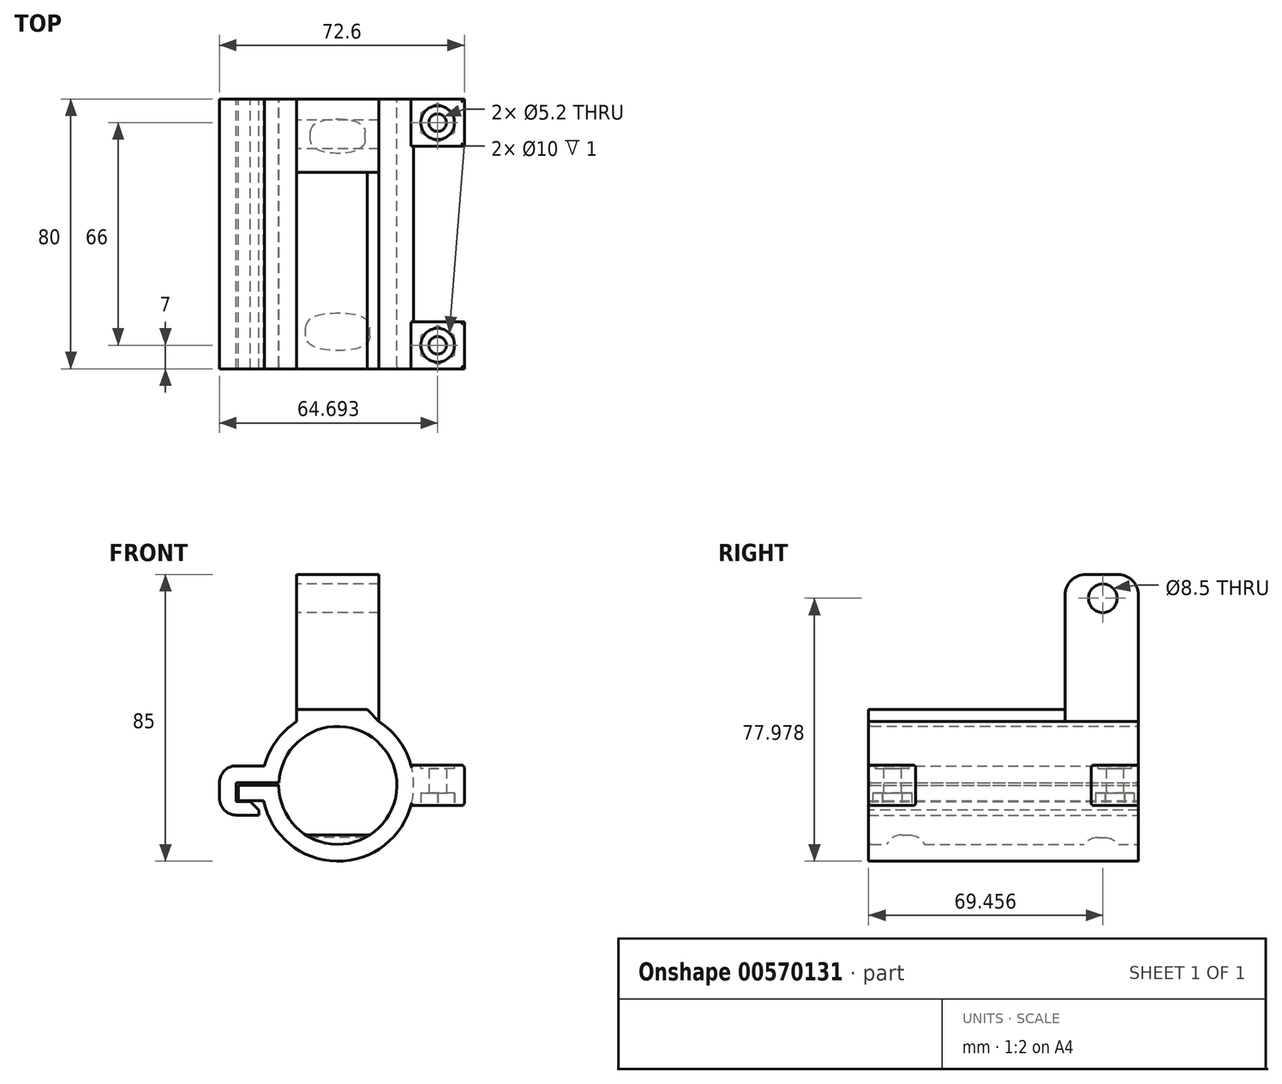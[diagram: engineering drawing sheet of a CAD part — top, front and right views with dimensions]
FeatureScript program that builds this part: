
annotation { "Feature Type Name" : "Feature", "Feature Type Description" : "" }
export const myFeature = defineFeature(function(context is Context, id is Id, definition is map)
    precondition{}
    {
        {
            var Q0;
            Q0=qCreatedBy(makeId("Front.planeOp"),FACE);
            var sketch = newSketch(context, id + "F0", { "sketchPlane" : qUnion([Q0])});
            skCircle(sketch, "E0", {"center": v(0, 0) * mm, "radius": 17.5 * mm});
            skCircle(sketch, "E1", {"center": v(0, 0) * mm, "radius": 22.5 * mm});
            skLineSegment(sketch, "E2", {"start": v(-22.5, 0) * mm, "end": v(22.5, 0) * mm});
            skLineSegment(sketch, "E3", {"start": v(22.5, 0) * mm, "end": v(37.5, 0) * mm});
            skLineSegment(sketch, "E4", {"start": v(37.5, 0) * mm, "end": v(37.5, -6) * mm});
            skLineSegment(sketch, "E5", {"start": v(37.5, -6) * mm, "end": v(21.69, -6) * mm});
            skLineSegment(sketch, "E6.MirrorCS", {"start": v(37.5, 6) * mm, "end": v(21.69, 6) * mm});
            skLineSegment(sketch, "E7.MirrorCS", {"start": v(37.5, 0) * mm, "end": v(37.5, 6) * mm});
            skLineSegment(sketch, "E8", {"start": v(-22.5, 0) * mm, "end": v(-29.5, 0) * mm});
            skLineSegment(sketch, "E9", {"start": v(-29.5, 0) * mm, "end": v(-29.5, -4.6) * mm});
            skLineSegment(sketch, "E10", {"start": v(-29.5, -4.6) * mm, "end": v(-22.02, -4.6) * mm});
            skLineSegment(sketch, "E11", {"start": v(-30.1, -4.8) * mm, "end": v(-30.1, 0.8) * mm});
            skLineSegment(sketch, "E12", {"start": v(-30.1, 0.8) * mm, "end": v(-22.49, 0.8) * mm});
            skLineSegment(sketch, "E13", {"start": v(-30.1, -4.8) * mm, "end": v(-23.4, -4.8) * mm});
            skLineSegment(sketch, "E14", {"start": v(-23.4, -4.8) * mm, "end": v(-23.4, -8.8) * mm});
            skLineSegment(sketch, "E15", {"start": v(-23.4, -8.8) * mm, "end": v(-35.1, -8.8) * mm});
            skLineSegment(sketch, "E16", {"start": v(-35.1, -8.8) * mm, "end": v(-35.1, 5.8) * mm});
            skLineSegment(sketch, "E17", {"start": v(-35.1, 5.8) * mm, "end": v(-21.74, 5.8) * mm});
            skLineSegment(sketch, "E18", {"start": v(-22.49, 0.8) * mm, "end": v(-17.48, 0.8) * mm});
            skSolve(sketch);
        }
        {
            var Q0;
            {var subQ0=sQuery(id+"F0.wireOp",EDGE,"E8");Q0=makeQuery(id+"F0.imprint","IMPRINT",FACE,{"disambiguationData":[TD([[makeQuery(id+"F0.imprint","IMPRINT",EDGE,{"derivedFrom":subQ0}),1.0]])]});}
            var Q1;
            {var subQ0=sQuery(id+"F0.wireOp",EDGE,"E2");var subQ6=sQuery(id+"F0.wireOp",EDGE,"E0");var subQ7=makeQuery(id+"F0.imprint","INTERSECT",VERTEX,{"disambiguationData":[OD(0.0)],"derivedFrom":[subQ6,subQ0]});Q1=makeQuery(id+"F0.imprint","IMPRINT",FACE,{"disambiguationData":[TD([[makeQuery(id+"F0.imprint","IMPRINT",EDGE,{"disambiguationData":[TD([[subQ7,1.0]])],"derivedFrom":subQ6}),-1.0]])]});}
            extrude(context, id + "F1", {"entities" : qUnion([Q0, Q1]), "depth" : 80 * mm, "offsetDistance" : 25 * mm});
        }
        {
            var Q0;
            Q0=makeQuery(id+"F0.imprint","IMPRINT",FACE,{"disambiguationData":[TD([[makeQuery(id+"F0.imprint","IMPRINT",EDGE,{"derivedFrom":sQuery(id+"F0.wireOp",EDGE,"E11")}),1.0]])]});
            var Q1;
            {var subQ5=sQuery(id+"F0.wireOp",EDGE,"E18");Q1=makeQuery(id+"F0.imprint","IMPRINT",FACE,{"disambiguationData":[TD([[makeQuery(id+"F0.imprint","IMPRINT",EDGE,{"derivedFrom":subQ5}),1.0]])]});}
            extrude(context, id + "F2", {"entities" : qUnion([Q0, Q1]), "depth" : 80 * mm, "offsetDistance" : 25 * mm});
        }
        {
            var Q0;
            {var subQ0=sQuery(id+"F0.wireOp",EDGE,"E3");Q0=makeQuery(id+"F0.imprint","IMPRINT",FACE,{"disambiguationData":[TD([[makeQuery(id+"F0.imprint","IMPRINT",EDGE,{"derivedFrom":subQ0}),1.0]])]});}
            extrude(context, id + "F3", {"entities" : qUnion([Q0]), "operationType" : NewBodyOperationType.ADD, "depth" : 80 * mm, "offsetDistance" : 25 * mm, "hasSecondDirection" : true, "secondDirectionOppositeDirection" : false, "secondDirectionDepth" : 66 * mm});
        }
        {
            var Q0;
            {var subQ0=sQuery(id+"F0.wireOp",EDGE,"E3");Q0=makeQuery(id+"F0.imprint","IMPRINT",FACE,{"disambiguationData":[TD([[makeQuery(id+"F0.imprint","IMPRINT",EDGE,{"derivedFrom":subQ0}),1.0]])]});}
            extrude(context, id + "F4", {"entities" : qUnion([Q0]), "operationType" : NewBodyOperationType.ADD, "depth" : 14 * mm, "offsetDistance" : 25 * mm});
        }
        {
            var Q0;
            Q0=makeQuery(id+"F0.imprint","IMPRINT",FACE,{"disambiguationData":[TD([[makeQuery(id+"F0.imprint","IMPRINT",EDGE,{"derivedFrom":sQuery(id+"F0.wireOp",EDGE,"E4")}),-1.0]])]});
            extrude(context, id + "F5", {"entities" : qUnion([Q0]), "operationType" : NewBodyOperationType.ADD, "depth" : 80 * mm, "offsetDistance" : 25 * mm, "hasSecondDirection" : true, "secondDirectionOppositeDirection" : false, "secondDirectionDepth" : 66 * mm});
        }
        {
            var Q0;
            Q0=makeQuery(id+"F0.imprint","IMPRINT",FACE,{"disambiguationData":[TD([[makeQuery(id+"F0.imprint","IMPRINT",EDGE,{"derivedFrom":sQuery(id+"F0.wireOp",EDGE,"E4")}),-1.0]])]});
            extrude(context, id + "F6", {"entities" : qUnion([Q0]), "operationType" : NewBodyOperationType.ADD, "depth" : 14 * mm, "offsetDistance" : 25 * mm});
        }
        {
            var Q0;
            Q0=qCreatedBy(makeId("Right.planeOp"),FACE);
            var sketch = newSketch(context, id + "F7", { "sketchPlane" : qUnion([Q0])});
            skLineSegment(sketch, "E19.0", {"start": v(-80, 0) * mm, "end": v(-80, -17.5) * mm});
            skLineSegment(sketch, "E20.0", {"start": v(0, -17.5) * mm, "end": v(0, 17.5) * mm});
            skLineSegment(sketch, "E21", {"start": v(-80, -17.5) * mm, "end": v(-69, -17.5) * mm});
            skLineSegment(sketch, "E22", {"start": v(-69, -17.5) * mm, "end": v(-69, -14.7) * mm});
            skLineSegment(sketch, "E23", {"start": v(-69, -14.7) * mm, "end": v(-63, -14.7) * mm});
            skLineSegment(sketch, "E24", {"start": v(-63, -14.7) * mm, "end": v(-63, -17.5) * mm});
            skLineSegment(sketch, "E25", {"start": v(-69, -14.7) * mm, "end": v(-75, -14.7) * mm});
            skLineSegment(sketch, "E26", {"start": v(-75, -14.7) * mm, "end": v(-75, -17.5) * mm});
            skLineSegment(sketch, "E27", {"start": v(-63, -17.5) * mm, "end": v(-69, -17.5) * mm});
            skLineSegment(sketch, "E28", {"start": v(0, -17.5) * mm, "end": v(-11, -17.5) * mm});
            skLineSegment(sketch, "E29", {"start": v(-11, -17.5) * mm, "end": v(-11, -15.5) * mm});
            skLineSegment(sketch, "E30", {"start": v(-11, -15.5) * mm, "end": v(-5, -15.5) * mm});
            skLineSegment(sketch, "E31", {"start": v(-11, -15.5) * mm, "end": v(-17, -15.5) * mm});
            skLineSegment(sketch, "E32", {"start": v(-17, -15.5) * mm, "end": v(-17, -17.5) * mm});
            skLineSegment(sketch, "E33", {"start": v(-17, -17.5) * mm, "end": v(-11, -17.5) * mm});
            skLineSegment(sketch, "E34", {"start": v(-5, -15.5) * mm, "end": v(-5, -17.5) * mm});
            skSolve(sketch);
        }
        {
            var Q0;
            {var subQ0=sQuery(id+"F7.wireOp",EDGE,"E22");Q0=makeQuery(id+"F7.imprint","IMPRINT",FACE,{"disambiguationData":[TD([[makeQuery(id+"F7.imprint","IMPRINT",EDGE,{"derivedFrom":subQ0}),1.0]])]});}
            var Q1;
            Q1=makeQuery(id+"F7.imprint","IMPRINT",FACE,{"disambiguationData":[TD([[makeQuery(id+"F7.imprint","IMPRINT",EDGE,{"derivedFrom":sQuery(id+"F7.wireOp",EDGE,"E22")}),-1.0]])]});
            var Q2;
            Q2=makeQuery(id+"F7.imprint","IMPRINT",FACE,{"disambiguationData":[TD([[makeQuery(id+"F7.imprint","IMPRINT",EDGE,{"derivedFrom":sQuery(id+"F7.wireOp",EDGE,"E29")}),1.0]])]});
            var Q3;
            {var subQ0=sQuery(id+"F7.wireOp",EDGE,"E29");Q3=makeQuery(id+"F7.imprint","IMPRINT",FACE,{"disambiguationData":[TD([[makeQuery(id+"F7.imprint","IMPRINT",EDGE,{"derivedFrom":subQ0}),-1.0]])]});}
            extrude(context, id + "F8", {"entities" : qUnion([Q0, Q1, Q2, Q3]), "operationType" : NewBodyOperationType.ADD, "depth" : 9.5 * mm, "offsetDistance" : 25 * mm, "hasSecondDirection" : true, "secondDirectionOppositeDirection" : true, "secondDirectionDepth" : 9.5 * mm});
        }
        {
            var Q0;
            Q0=makeQuery(id+"F8.opExtrude","SWEPT_EDGE",EDGE,{"disambiguationData":[OSD([sQuery(id+"F7.wireOp",EDGE,"E25"),sQuery(id+"F7.wireOp",EDGE,"E26")])]});
            var Q1;
            Q1=makeQuery(id+"F8.opExtrude","SWEPT_EDGE",EDGE,{"disambiguationData":[OSD([sQuery(id+"F7.wireOp",EDGE,"E23"),sQuery(id+"F7.wireOp",EDGE,"E24")])]});
            var Q2;
            Q2=makeQuery(id+"F8.opExtrude","SWEPT_EDGE",EDGE,{"disambiguationData":[OSD([sQuery(id+"F7.wireOp",EDGE,"E31"),sQuery(id+"F7.wireOp",EDGE,"E32")])]});
            var Q3;
            Q3=makeQuery(id+"F8.opExtrude","SWEPT_EDGE",EDGE,{"disambiguationData":[OSD([sQuery(id+"F7.wireOp",EDGE,"E30"),sQuery(id+"F7.wireOp",EDGE,"E34")])]});
            fillet(context, id + "F9", {"entities" : qUnion([Q0, Q1, Q2, Q3]), "radius" : 4.8 * mm, "tangentPropagation" : true, "allowEdgeOverflow" : false});
        }
        {
            var Q0;
            Q0=makeQuery(id+"F5.opExtrude","SWEPT_FACE",FACE,{"disambiguationData":[OSD([sQuery(id+"F0.wireOp",EDGE,"E5")])]});
            var sketch = newSketch(context, id + "F10", { "sketchPlane" : qUnion([Q0])});
            skLineSegment(sketch, "E35", {"start": v(29.6, 80) * mm, "end": v(29.6, 66) * mm});
            skCircle(sketch, "E36.cCircle", {"center": v(29.6, 73) * mm, "radius": 5 * mm, "construction": true});
            skLineSegment(sketch, "E36.0", {"start": v(29.65, 78.77) * mm, "end": v(34.62, 75.84) * mm});
            skLineSegment(sketch, "E36.1", {"start": v(34.62, 75.84) * mm, "end": v(34.57, 70.07) * mm});
            skLineSegment(sketch, "E36.2", {"start": v(34.57, 70.07) * mm, "end": v(29.54, 67.23) * mm});
            skLineSegment(sketch, "E36.3", {"start": v(29.54, 67.23) * mm, "end": v(24.57, 70.16) * mm});
            skLineSegment(sketch, "E36.4", {"start": v(24.57, 70.16) * mm, "end": v(24.62, 75.93) * mm});
            skLineSegment(sketch, "E36.5", {"start": v(24.62, 75.93) * mm, "end": v(29.65, 78.77) * mm});
            skPoint(sketch, "E36.0.midPoint", {"position": v(32.13, 77.3) * mm});
            skCircle(sketch, "E37", {"center": v(29.6, 73) * mm, "radius": 2.6 * mm});
            skSolve(sketch);
        }
        {
            var Q0;
            Q0=makeQuery(id+"F6.opExtrude","SWEPT_FACE",FACE,{"disambiguationData":[OSD([sQuery(id+"F0.wireOp",EDGE,"E5")])]});
            var sketch = newSketch(context, id + "F11", { "sketchPlane" : qUnion([Q0])});
            skLineSegment(sketch, "E38", {"start": v(29.6, 14) * mm, "end": v(29.6, 0) * mm});
            skCircle(sketch, "E39.cCircle", {"center": v(29.6, 7) * mm, "radius": 5 * mm, "construction": true});
            skLineSegment(sketch, "E39.0", {"start": v(29.64, 12.77) * mm, "end": v(34.62, 9.85) * mm});
            skLineSegment(sketch, "E39.1", {"start": v(34.62, 9.85) * mm, "end": v(34.57, 4.07) * mm});
            skLineSegment(sketch, "E39.2", {"start": v(34.57, 4.07) * mm, "end": v(29.54, 1.23) * mm});
            skLineSegment(sketch, "E39.3", {"start": v(29.54, 1.23) * mm, "end": v(24.57, 4.15) * mm});
            skLineSegment(sketch, "E39.4", {"start": v(24.57, 4.15) * mm, "end": v(24.62, 9.93) * mm});
            skLineSegment(sketch, "E39.5", {"start": v(24.62, 9.93) * mm, "end": v(29.64, 12.77) * mm});
            skPoint(sketch, "E39.0.midPoint", {"position": v(32.13, 11.3) * mm});
            skCircle(sketch, "E40", {"center": v(29.6, 7) * mm, "radius": 2.6 * mm});
            skSolve(sketch);
        }
        {
            var Q0;
            {var subQ4=sQuery(id+"F10.wireOp",EDGE,"E36.0");Q0=makeQuery(id+"F10.imprint","IMPRINT",FACE,{"disambiguationData":[TD([[makeQuery(id+"F10.imprint","IMPRINT",EDGE,{"derivedFrom":subQ4}),-1.0]])]});}
            var Q1;
            {var subQ1=sQuery(id+"F10.wireOp",EDGE,"E36.3");Q1=makeQuery(id+"F10.imprint","IMPRINT",FACE,{"disambiguationData":[TD([[makeQuery(id+"F10.imprint","IMPRINT",EDGE,{"derivedFrom":subQ1}),-1.0]])]});}
            var Q2;
            {var subQ4=sQuery(id+"F11.wireOp",EDGE,"E39.0");Q2=makeQuery(id+"F11.imprint","IMPRINT",FACE,{"disambiguationData":[TD([[makeQuery(id+"F11.imprint","IMPRINT",EDGE,{"derivedFrom":subQ4}),-1.0]])]});}
            var Q3;
            {var subQ1=sQuery(id+"F11.wireOp",EDGE,"E39.3");Q3=makeQuery(id+"F11.imprint","IMPRINT",FACE,{"disambiguationData":[TD([[makeQuery(id+"F11.imprint","IMPRINT",EDGE,{"derivedFrom":subQ1}),-1.0]])]});}
            extrude(context, id + "F12", {"entities" : qUnion([Q0, Q1, Q2, Q3]), "operationType" : NewBodyOperationType.REMOVE, "oppositeDirection" : true, "depth" : 3.8 * mm, "offsetDistance" : 25 * mm});
        }
        {
            var Q0;
            Q0=makeQuery(id+"F12.boolean.opBoolean","SPLIT",FACE,{"disambiguationData":[TD([makeQuery(id+"F12.opExtrude","SWEPT_FACE",FACE,{"disambiguationData":[OSD([sQuery(id+"F10.wireOp",EDGE,"E37")])]})])],"derivedFrom":makeQuery(id+"F5.opExtrude","SWEPT_FACE",FACE,{"disambiguationData":[OSD([sQuery(id+"F0.wireOp",EDGE,"E5")])]})});
            var Q1;
            Q1=makeQuery(id+"F12.boolean.opBoolean","SPLIT",FACE,{"disambiguationData":[TD([makeQuery(id+"F12.opExtrude","SWEPT_FACE",FACE,{"disambiguationData":[OSD([sQuery(id+"F11.wireOp",EDGE,"E40")])]})])],"derivedFrom":makeQuery(id+"F6.opExtrude","SWEPT_FACE",FACE,{"disambiguationData":[OSD([sQuery(id+"F0.wireOp",EDGE,"E5")])]})});
            extrude(context, id + "F13", {"entities" : qUnion([Q0, Q1]), "operationType" : NewBodyOperationType.REMOVE, "endBound" : BoundingType.THROUGH_ALL, "oppositeDirection" : true, "depth" : 25 * mm, "offsetDistance" : 25 * mm});
        }
        {
            var Q0;
            Q0=makeQuery(id+"F3.opExtrude","SWEPT_FACE",FACE,{"disambiguationData":[OSD([sQuery(id+"F0.wireOp",EDGE,"E6.MirrorCS")])]});
            var sketch = newSketch(context, id + "F14", { "sketchPlane" : qUnion([Q0])});
            skCircle(sketch, "E41", {"center": v(29.6, -73) * mm, "radius": 5 * mm});
            skSolve(sketch);
        }
        {
            var Q0;
            Q0=makeQuery(id+"F4.opExtrude","SWEPT_FACE",FACE,{"disambiguationData":[OSD([sQuery(id+"F0.wireOp",EDGE,"E6.MirrorCS")])]});
            var sketch = newSketch(context, id + "F15", { "sketchPlane" : qUnion([Q0])});
            skCircle(sketch, "E42", {"center": v(29.6, -7) * mm, "radius": 5 * mm});
            skSolve(sketch);
        }
        {
            var Q0;
            Q0=makeQuery(id+"F15.imprint","IMPRINT",FACE,{"disambiguationData":[TD([[makeQuery(id+"F15.imprint","IMPRINT",EDGE,{"derivedFrom":sQuery(id+"F15.wireOp",EDGE,"E42")}),1.0]])]});
            var Q1;
            Q1=makeQuery(id+"F14.imprint","IMPRINT",FACE,{"disambiguationData":[TD([[makeQuery(id+"F14.imprint","IMPRINT",EDGE,{"derivedFrom":sQuery(id+"F14.wireOp",EDGE,"E41")}),1.0]])]});
            extrude(context, id + "F16", {"entities" : qUnion([Q0, Q1]), "operationType" : NewBodyOperationType.REMOVE, "oppositeDirection" : true, "depth" : 1 * mm, "offsetDistance" : 25 * mm});
        }
        {
            var Q0;
            Q0=makeQuery(id+"F2.opExtrude","SWEPT_EDGE",EDGE,{"disambiguationData":[OSD([sQuery(id+"F0.wireOp",EDGE,"E16"),sQuery(id+"F0.wireOp",EDGE,"E17")])]});
            var Q1;
            Q1=makeQuery(id+"F2.opExtrude","SWEPT_EDGE",EDGE,{"disambiguationData":[OSD([sQuery(id+"F0.wireOp",EDGE,"E15"),sQuery(id+"F0.wireOp",EDGE,"E16")])]});
            fillet(context, id + "F17", {"entities" : qUnion([Q0, Q1]), "radius" : 5 * mm, "tangentPropagation" : true, "allowEdgeOverflow" : false});
        }
        {
            var Q0;
            Q0=makeQuery(id+"F2.opExtrude","SWEPT_EDGE",EDGE,{"disambiguationData":[OSD([sQuery(id+"F0.wireOp",EDGE,"E13"),sQuery(id+"F0.wireOp",EDGE,"E14")])]});
            chamfer(context, id + "F18", {"entities" : qUnion([Q0]), "width" : 2.5 * mm, "tangentPropagation" : true});
        }
        {
            var Q0;
            Q0=makeQuery(id+"F3.opExtrude","CAP_EDGE",EDGE,{"disambiguationData":[OSD([sQuery(id+"F0.wireOp",EDGE,"E6.MirrorCS")])],"isStart":false});
            var Q1;
            Q1=makeQuery(id+"F3.opExtrude","SWEPT_EDGE",EDGE,{"disambiguationData":[OSD([sQuery(id+"F0.wireOp",EDGE,"E6.MirrorCS"),sQuery(id+"F0.wireOp",EDGE,"E7.MirrorCS")])]});
            var Q2;
            Q2=makeQuery(id+"F5.opExtrude","CAP_EDGE",EDGE,{"disambiguationData":[OSD([sQuery(id+"F0.wireOp",EDGE,"E5")])],"isStart":false});
            var Q3;
            Q3=makeQuery(id+"F5.opExtrude","SWEPT_EDGE",EDGE,{"disambiguationData":[OSD([sQuery(id+"F0.wireOp",EDGE,"E4"),sQuery(id+"F0.wireOp",EDGE,"E5")])]});
            var Q4;
            Q4=makeQuery(id+"F5.opExtrude","CAP_EDGE",EDGE,{"disambiguationData":[OSD([sQuery(id+"F0.wireOp",EDGE,"E5")])],"isStart":true});
            var Q5;
            Q5=makeQuery(id+"F3.opExtrude","CAP_EDGE",EDGE,{"disambiguationData":[OSD([sQuery(id+"F0.wireOp",EDGE,"E6.MirrorCS")])],"isStart":true});
            var Q6;
            Q6=makeQuery(id+"F4.opExtrude","CAP_EDGE",EDGE,{"disambiguationData":[OSD([sQuery(id+"F0.wireOp",EDGE,"E6.MirrorCS")])],"isStart":false});
            var Q7;
            Q7=makeQuery(id+"F4.opExtrude","SWEPT_EDGE",EDGE,{"disambiguationData":[OSD([sQuery(id+"F0.wireOp",EDGE,"E6.MirrorCS"),sQuery(id+"F0.wireOp",EDGE,"E7.MirrorCS")])]});
            var Q8;
            Q8=makeQuery(id+"F4.opExtrude","CAP_EDGE",EDGE,{"disambiguationData":[OSD([sQuery(id+"F0.wireOp",EDGE,"E6.MirrorCS")])],"isStart":true});
            var Q9;
            Q9=makeQuery(id+"F6.opExtrude","CAP_EDGE",EDGE,{"disambiguationData":[OSD([sQuery(id+"F0.wireOp",EDGE,"E5")])],"isStart":true});
            var Q10;
            Q10=makeQuery(id+"F6.opExtrude","SWEPT_EDGE",EDGE,{"disambiguationData":[OSD([sQuery(id+"F0.wireOp",EDGE,"E4"),sQuery(id+"F0.wireOp",EDGE,"E5")])]});
            var Q11;
            Q11=makeQuery(id+"F6.opExtrude","CAP_EDGE",EDGE,{"disambiguationData":[OSD([sQuery(id+"F0.wireOp",EDGE,"E5")])],"isStart":false});
            var Q12;
            Q12=makeQuery(id+"F1.opExtrude","CAP_EDGE",EDGE,{"disambiguationData":[OSD([sQuery(id+"F0.wireOp",EDGE,"E0")])],"isStart":true});
            var Q13;
            Q13=makeQuery(id+"F2.opExtrude","CAP_EDGE",EDGE,{"disambiguationData":[OSD([sQuery(id+"F0.wireOp",EDGE,"E0")])],"isStart":true});
            var Q14;
            Q14=makeQuery(id+"F2.opExtrude","CAP_EDGE",EDGE,{"disambiguationData":[OSD([sQuery(id+"F0.wireOp",EDGE,"E0")])],"isStart":false});
            var Q15;
            Q15=makeQuery(id+"F1.opExtrude","CAP_EDGE",EDGE,{"disambiguationData":[OSD([sQuery(id+"F0.wireOp",EDGE,"E0")])],"isStart":false});
            fillet(context, id + "F19", {"entities" : qUnion([Q0, Q1, Q2, Q3, Q4, Q5, Q6, Q7, Q8, Q9, Q10, Q11, Q12, Q13, Q14, Q15]), "radius" : .8 * mm, "tangentPropagation" : true, "allowEdgeOverflow" : false});
        }
        {
            var Q0;
            Q0=qCreatedBy(makeId("Front.planeOp"),FACE);
            var sketch = newSketch(context, id + "F20", { "sketchPlane" : qUnion([Q0])});
            skCircle(sketch, "E43.0", {"center": v(0, 0) * mm, "radius": 22.5 * mm});
            skLineSegment(sketch, "E44", {"start": v(-12.2, 62.5) * mm, "end": v(-12.2, 18.9) * mm});
            skLineSegment(sketch, "E45", {"start": v(12.2, 62.5) * mm, "end": v(12.2, 18.9) * mm});
            skLineSegment(sketch, "E46", {"start": v(-12.2, 62.5) * mm, "end": v(12.2, 62.5) * mm});
            skSolve(sketch);
        }
        {
            var Q0;
            {var subQ0=sQuery(id+"F20.wireOp",EDGE,"E44");Q0=makeQuery(id+"F20.imprint","IMPRINT",FACE,{"disambiguationData":[TD([[makeQuery(id+"F20.imprint","IMPRINT",EDGE,{"derivedFrom":subQ0}),1.0]])]});}
            extrude(context, id + "F21", {"entities" : qUnion([Q0]), "operationType" : NewBodyOperationType.ADD, "depth" : 80 * mm, "offsetDistance" : 25 * mm});
        }
        {
            var Q0;
            Q0=makeQuery(id+"F21.opExtrude","SWEPT_FACE",FACE,{"disambiguationData":[OSD([sQuery(id+"F20.wireOp",EDGE,"E44")])]});
            var sketch = newSketch(context, id + "F22", { "sketchPlane" : qUnion([Q0])});
            skLineSegment(sketch, "E47.0", {"start": v(0, 22.5) * mm, "end": v(0, -22.5) * mm});
            skCircle(sketch, "E48", {"center": v(10.54, 55.48) * mm, "radius": 4.25 * mm});
            skLineSegment(sketch, "E49", {"start": v(0, 22.5) * mm, "end": v(0, 56.5) * mm});
            skLineSegment(sketch, "E50", {"start": v(6, 62.5) * mm, "end": v(15.7, 62.5) * mm});
            skLineSegment(sketch, "E51", {"start": v(21.7, 56.5) * mm, "end": v(21.7, 18.9) * mm});
            skPoint(sketch, "E52.visualSharp", {"position": v(21.7, 62.5) * mm});
            skArc(sketch, "E52.filletArc", {"start": v(21.7, 56.5) * mm, "mid": v(19.94, 60.74) * mm, "end": v(15.7, 62.5) * mm});
            skPoint(sketch, "E53.visualSharp", {"position": v(0, 62.5) * mm});
            skArc(sketch, "E53.filletArc", {"start": v(6, 62.5) * mm, "mid": v(1.76, 60.74) * mm, "end": v(0, 56.5) * mm});
            skLineSegment(sketch, "E54", {"start": v(0, 22.5) * mm, "end": v(80, 22.5) * mm});
            skSolve(sketch);
        }
        {
            var Q0;
            Q0=makeQuery(id+"F22.imprint","IMPRINT",FACE,{"disambiguationData":[TD([[makeQuery(id+"F22.imprint","IMPRINT",EDGE,{"derivedFrom":sQuery(id+"F22.wireOp",EDGE,"j48K2Env-jYCd-4d7W-JV06-Xabx8kKvVo21")}),-1.0]])]});
            var Q1;
            {var subQ0=sQuery(id+"F22.wireOp",EDGE,"ZgvWATYV-ukQq-1yaV-QLWK-iv909JYuOCem");Q1=makeQuery(id+"F22.imprint","IMPRINT",FACE,{"disambiguationData":[TD([[makeQuery(id+"F22.imprint","IMPRINT",EDGE,{"derivedFrom":subQ0}),-1.0]])]});}
            var Q2;
            {var subQ3=sQuery(id+"F22.wireOp",EDGE,"BhtDEUDy-caWM-ZsNg-1Gep-qLVb42udASMh");Q2=makeQuery(id+"F22.imprint","IMPRINT",FACE,{"disambiguationData":[TD([[makeQuery(id+"F22.imprint","IMPRINT",EDGE,{"derivedFrom":subQ3}),-1.0]])]});}
            var Q3;
            {var subQ0=sQuery(id+"F22.wireOp",EDGE,"BhtDEUDy-caWM-ZsNg-1Gep-qLVb42udASMh");Q3=makeQuery(id+"F22.imprint","IMPRINT",FACE,{"disambiguationData":[TD([[makeQuery(id+"F22.imprint","IMPRINT",EDGE,{"derivedFrom":subQ0}),1.0]])]});}
            var Q4;
            Q4=makeQuery(id+"F22.imprint","IMPRINT",FACE,{"disambiguationData":[TD([[makeQuery(id+"F22.imprint","IMPRINT",EDGE,{"derivedFrom":sQuery(id+"F22.wireOp",EDGE,"E48")}),1.0]])]});
            var Q5;
            {var subQ0=sQuery(id+"F22.wireOp",EDGE,"E53.filletArc");Q5=makeQuery(id+"F22.imprint","IMPRINT",FACE,{"disambiguationData":[TD([[makeQuery(id+"F22.imprint","IMPRINT",EDGE,{"derivedFrom":subQ0}),-1.0]])]});}
            var Q6;
            {var subQ4=sQuery(id+"F22.wireOp",EDGE,"E52.filletArc");Q6=makeQuery(id+"F22.imprint","IMPRINT",FACE,{"disambiguationData":[TD([[makeQuery(id+"F22.imprint","IMPRINT",EDGE,{"derivedFrom":subQ4}),-1.0]])]});}
            extrude(context, id + "F23", {"entities" : qUnion([Q0, Q1, Q2, Q3, Q4, Q5, Q6]), "operationType" : NewBodyOperationType.REMOVE, "endBound" : BoundingType.THROUGH_ALL, "oppositeDirection" : true, "depth" : 25 * mm, "offsetDistance" : 25 * mm});
        }
        {
            var Q0;
            Q0=makeQuery(id+"F23.boolean.opBoolean","COPY",EDGE,{"derivedFrom":makeQuery(id+"F23.opExtrude","CAP_EDGE",EDGE,{"disambiguationData":[OSD([sQuery(id+"F22.wireOp",EDGE,"E54")])],"isStart":true})});
            var Q1;
            Q1=makeQuery(id+"F23.boolean.opBoolean","INTERSECT",EDGE,{"derivedFrom":[makeQuery(id+"F21.opExtrude","SWEPT_FACE",FACE,{"disambiguationData":[OSD([sQuery(id+"F20.wireOp",EDGE,"E45")])]}),makeQuery(id+"F23.opExtrude","SWEPT_FACE",FACE,{"disambiguationData":[OSD([sQuery(id+"F22.wireOp",EDGE,"E54")])]})]});
            chamfer(context, id + "F24", {"entities" : qUnion([Q0, Q1]), "width" : 3.5 * mm, "tangentPropagation" : true});
        }
    });
